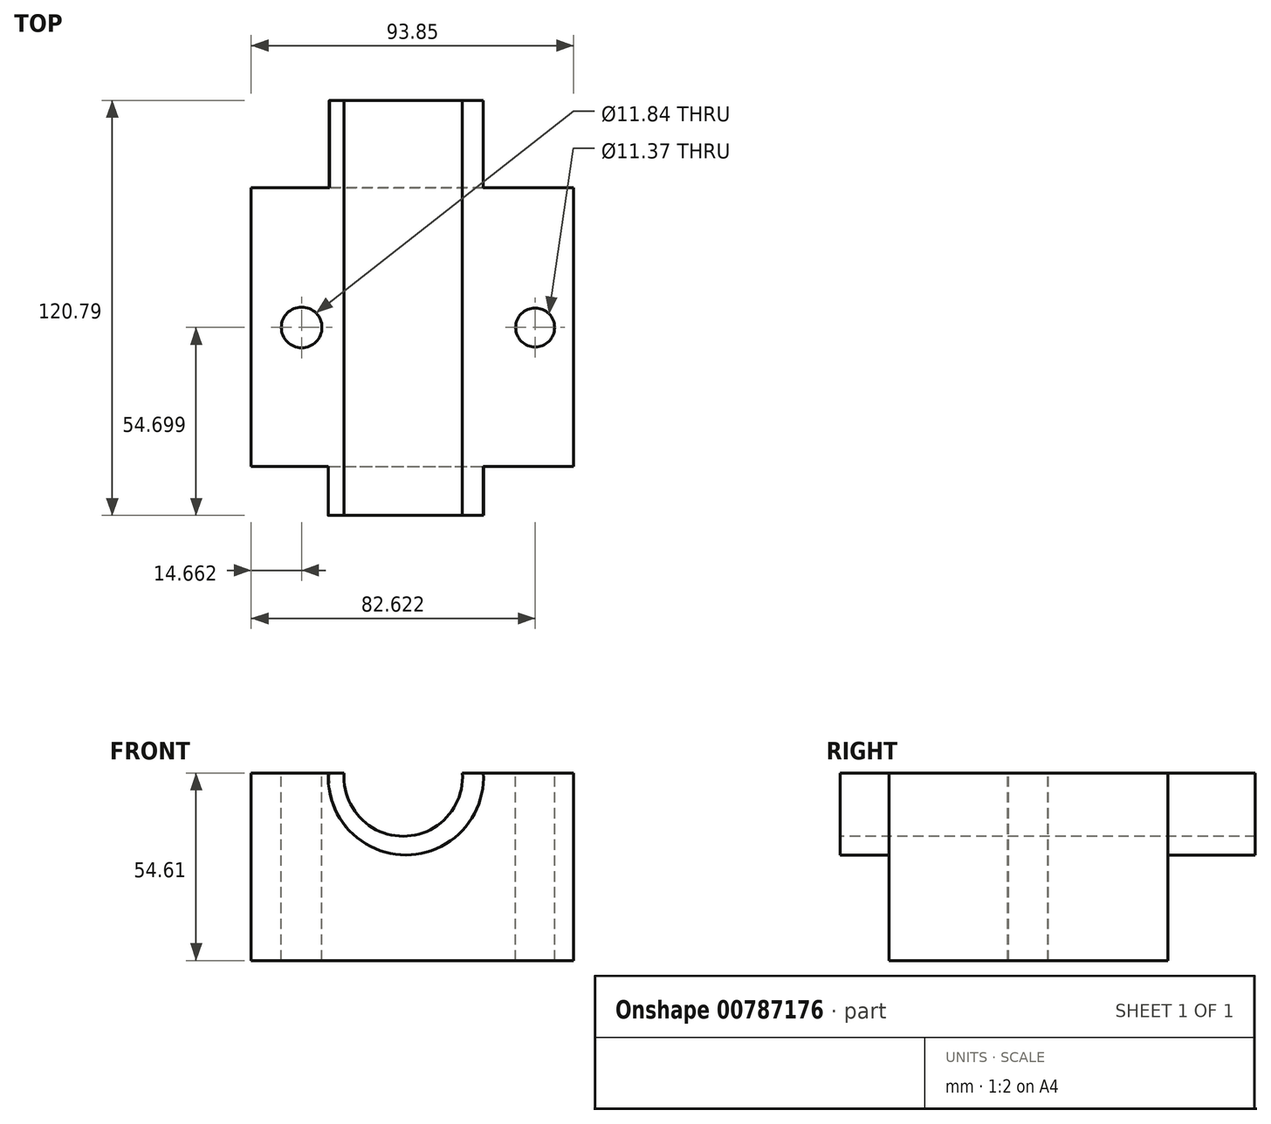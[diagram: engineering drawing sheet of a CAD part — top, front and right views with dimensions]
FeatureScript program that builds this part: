
annotation { "Feature Type Name" : "Feature", "Feature Type Description" : "" }
export const myFeature = defineFeature(function(context is Context, id is Id, definition is map)
    precondition{}
    {
        {
            var Q0;
            Q0=qCreatedBy(makeId("Top.planeOp"),FACE);
            var sketch = newSketch(context, id + "F0", { "sketchPlane" : qUnion([Q0])});
            skLineSegment(sketch, "E0.bottom", {"start": v(-53.1, 54.26) * mm, "end": v(40.75, 54.26) * mm});
            skLineSegment(sketch, "E0.top", {"start": v(-53.1, -26.9) * mm, "end": v(40.75, -26.9) * mm});
            skLineSegment(sketch, "E0.left", {"start": v(-53.1, 54.26) * mm, "end": v(-53.1, -26.9) * mm});
            skLineSegment(sketch, "E0.right", {"start": v(40.75, 54.26) * mm, "end": v(40.75, -26.9) * mm});
            skSolve(sketch);
        }
        {
            var Q0;
            Q0 = qSketchRegion(id + "F0", true);
            extrude(context, id + "F1", {"entities" : qUnion([Q0]), "depth" : 54.6 * mm, "offsetDistance" : 25.4 * mm});
        }
        {
            var Q0;
            Q0=makeQuery(id+"F1.opExtrude","SWEPT_FACE",FACE,{"disambiguationData":[OSD([sQuery(id+"F0.wireOp",EDGE,"E0.top")])]});
            var sketch = newSketch(context, id + "F2", { "sketchPlane" : qUnion([Q0])});
            skArc(sketch, "E1", {"start": v(-30.67, 54.6) * mm, "mid": v(-8.11, 30.74) * mm, "end": v(14.44, 54.6) * mm});
            skArc(sketch, "E2", {"start": v(-26.1, 54.6) * mm, "mid": v(-8.87, 36.19) * mm, "end": v(8.35, 54.61) * mm});
            skLineSegment(sketch, "E3", {"start": v(-30.67, 54.61) * mm, "end": v(14.44, 54.61) * mm});
            skSolve(sketch);
        }
        {
            var Q0;
            {var subQ0=sQuery(id+"F2.wireOp",EDGE,"E2");Q0=makeQuery(id+"F2.imprint","IMPRINT",FACE,{"disambiguationData":[TD([[makeQuery(id+"F2.imprint","IMPRINT",EDGE,{"derivedFrom":subQ0}),1.0]])]});}
            extrude(context, id + "F3", {"entities" : qUnion([Q0]), "operationType" : NewBodyOperationType.REMOVE, "oppositeDirection" : true, "depth" : 106.43 * mm, "offsetDistance" : 25.4 * mm});
        }
        {
            var Q0;
            {var subQ0=sQuery(id+"F2.wireOp",EDGE,"E1");Q0=makeQuery(id+"F2.imprint","IMPRINT",FACE,{"disambiguationData":[TD([[makeQuery(id+"F2.imprint","IMPRINT",EDGE,{"derivedFrom":subQ0}),1.0]])]});}
            extrude(context, id + "F4", {"entities" : qUnion([Q0]), "operationType" : NewBodyOperationType.ADD, "depth" : 14.22 * mm, "offsetDistance" : 25.4 * mm});
        }
        {
            var Q0;
            Q0=makeQuery(id+"F1.opExtrude","SWEPT_FACE",FACE,{"disambiguationData":[OSD([sQuery(id+"F0.wireOp",EDGE,"E0.bottom")])]});
            var sketch = newSketch(context, id + "F5", { "sketchPlane" : qUnion([Q0])});
            skArc(sketch, "E4", {"start": v(-14.41, 54.6) * mm, "mid": v(7.96, 30.67) * mm, "end": v(30.34, 54.6) * mm});
            skSolve(sketch);
        }
        {
            var Q0;
            {var subQ0=sQuery(id+"F5.wireOp",EDGE,"E4");Q0=makeQuery(id+"F5.imprint","IMPRINT",FACE,{"disambiguationData":[TD([[makeQuery(id+"F5.imprint","IMPRINT",EDGE,{"derivedFrom":subQ0}),1.0]])]});}
            extrude(context, id + "F6", {"entities" : qUnion([Q0]), "operationType" : NewBodyOperationType.ADD, "depth" : 25.4 * mm, "offsetDistance" : 25.4 * mm});
        }
        {
            var Q0;
            {var subQ0=sQuery(id+"F0.wireOp",EDGE,"E0.bottom");var subQ2=sQuery(id+"F0.wireOp",EDGE,"E0.left");var subQ3=sQuery(id+"F0.wireOp",EDGE,"E0.top");var subQ4=makeQuery(id+"F1.opExtrude","CAP_FACE",FACE,{"disambiguationData":[OSD([subQ0,subQ3,subQ2,sQuery(id+"F0.wireOp",EDGE,"E0.right")])],"isStart":false});var subQ5=makeQuery(id+"F1.opExtrude","SWEPT_FACE",FACE,{"disambiguationData":[OSD([subQ2])]});var subQ6=sQuery(id+"F2.wireOp",EDGE,"E2");var subQ8=makeQuery(id+"F3.boolean.opBoolean","SPLIT",EDGE,{"disambiguationData":[TD([subQ5])],"derivedFrom":makeQuery(id+"F1.opExtrude","CAP_EDGE",EDGE,{"disambiguationData":[OSD([subQ0])],"isStart":false})});var subQ9=sQuery(id+"F2.wireOp",EDGE,"E3");Q0=makeQuery(id+"F6.boolean.opBoolean","MERGE",FACE,{"derivedFrom":[makeQuery(id+"F4.boolean.opBoolean","MERGE",FACE,{"derivedFrom":[makeQuery(id+"F3.boolean.opBoolean","SPLIT",FACE,{"disambiguationData":[TD([subQ5])],"derivedFrom":subQ4}),makeQuery(id+"F4.opExtrude","SWEPT_FACE",FACE,{"disambiguationData":[OSD([subQ9]),TDD([makeQuery(id+"F2.imprint","IMPRINT",EDGE,{"disambiguationData":[TD([[makeQuery(id+"F2.imprint","INTERSECT",VERTEX,{"disambiguationData":[OD(0.0)],"derivedFrom":[subQ6,subQ9]}),1.0]])],"derivedFrom":subQ9})])]})]}),makeQuery(id+"F6.opExtrude","SWEPT_FACE",FACE,{"disambiguationData":[OSD([subQ0]),TDD([makeQuery(id+"F5.imprint","IMPRINT",EDGE,{"disambiguationData":[TD([[makeQuery(id+"F5.imprint","INTERSECT",VERTEX,{"derivedFrom":[subQ8,sQuery(id+"F5.wireOp",EDGE,"E4")]}),-1.0]])],"derivedFrom":subQ8})])]})]});}
            var sketch = newSketch(context, id + "F7", { "sketchPlane" : qUnion([Q0])});
            skCircle(sketch, "E5", {"center": v(29.52, 13.57) * mm, "radius": 5.68 * mm});
            skCircle(sketch, "E6", {"center": v(-38.44, 13.57) * mm, "radius": 5.92 * mm});
            skSolve(sketch);
        }
        {
            var Q0;
            Q0 = qSketchRegion(id + "F7", true);
            extrude(context, id + "F8", {"entities" : qUnion([Q0]), "operationType" : NewBodyOperationType.REMOVE, "oppositeDirection" : true, "depth" : 85.6 * mm, "offsetDistance" : 25.4 * mm});
        }
    });
